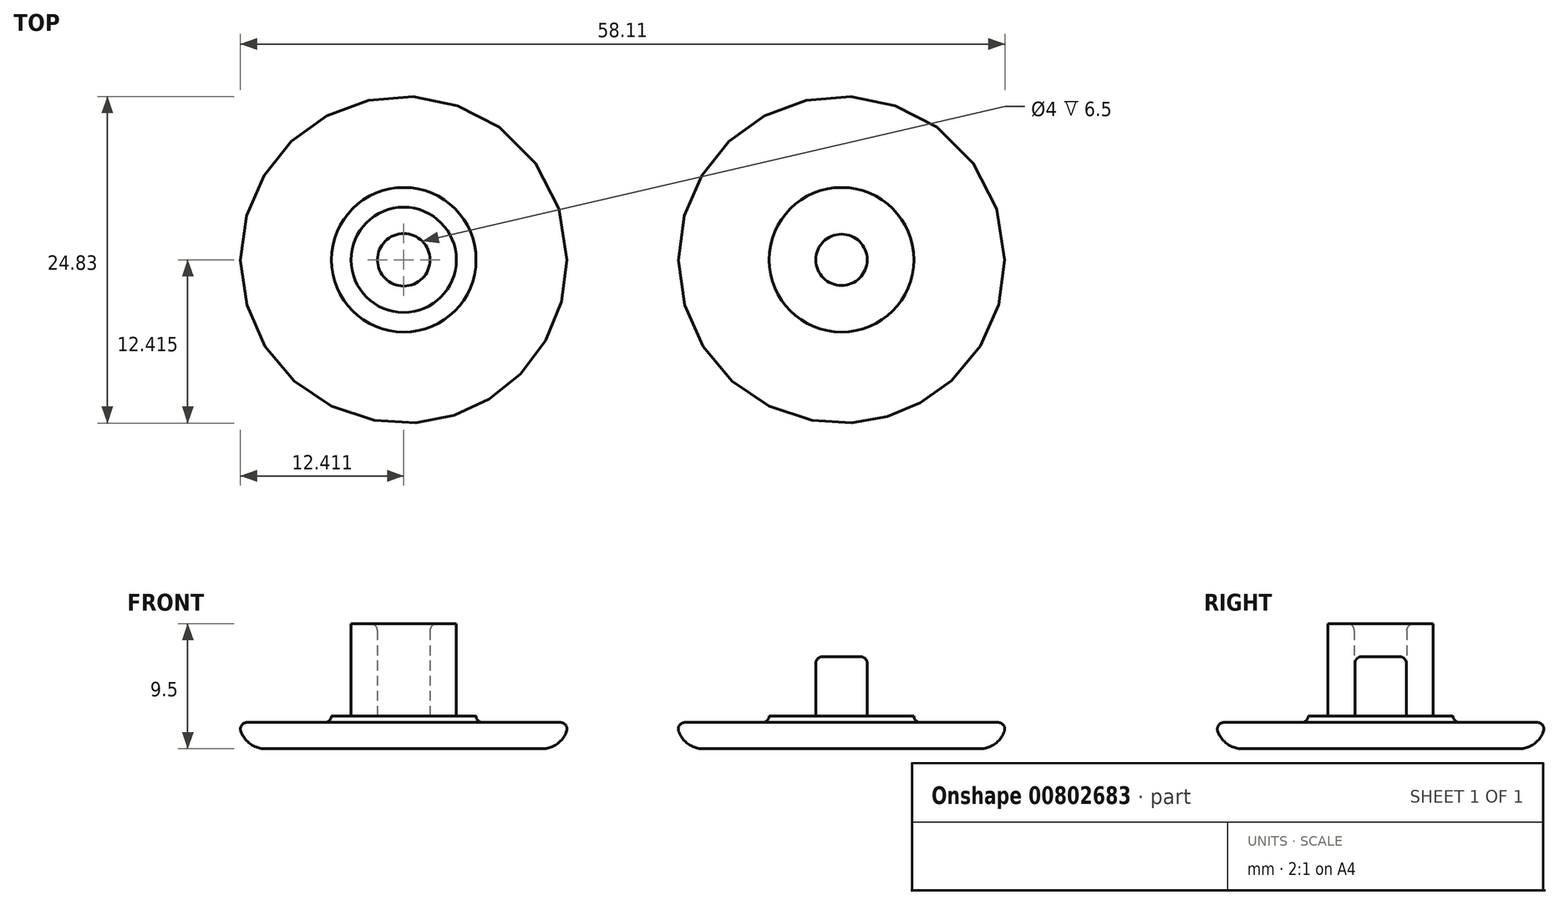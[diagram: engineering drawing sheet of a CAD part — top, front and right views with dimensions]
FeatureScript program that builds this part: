
annotation { "Feature Type Name" : "Feature", "Feature Type Description" : "" }
export const myFeature = defineFeature(function(context is Context, id is Id, definition is map)
    precondition{}
    {
        {
            var Q0;
            Q0=qCreatedBy(makeId("Top.planeOp"),FACE);
            var sketch = newSketch(context, id + "F0", { "sketchPlane" : qUnion([Q0])});
            skCircle(sketch, "E0", {"center": v(-165.76, 137.5) * mm, "radius": 12.5 * mm});
            skCircle(sketch, "E1", {"center": v(-132.48, 137.5) * mm, "radius": 12.5 * mm});
            skCircle(sketch, "E2", {"center": v(-165.76, 137.5) * mm, "radius": 5.5 * mm});
            skCircle(sketch, "E3", {"center": v(-165.76, 137.5) * mm, "radius": 4 * mm});
            skCircle(sketch, "E4", {"center": v(-165.76, 137.5) * mm, "radius": 2 * mm});
            skCircle(sketch, "E5", {"center": v(-132.48, 137.5) * mm, "radius": 5.5 * mm});
            skCircle(sketch, "E6", {"center": v(-132.48, 137.5) * mm, "radius": 1.95 * mm});
            skSolve(sketch);
        }
        {
            var Q0;
            Q0=makeQuery(id+"F0.imprint","IMPRINT",FACE,{"disambiguationData":[TD([[makeQuery(id+"F0.imprint","IMPRINT",EDGE,{"derivedFrom":sQuery(id+"F0.wireOp",EDGE,"E0")}),1.0]])]});
            var Q1;
            Q1=makeQuery(id+"F0.imprint","IMPRINT",FACE,{"disambiguationData":[TD([[makeQuery(id+"F0.imprint","IMPRINT",EDGE,{"derivedFrom":sQuery(id+"F0.wireOp",EDGE,"E1")}),1.0]])]});
            extrude(context, id + "F1", {"entities" : qUnion([Q0, Q1]), "depth" : 2 * mm, "offsetDistance" : 25 * mm});
        }
        {
            var Q0;
            Q0=makeQuery(id+"F0.imprint","IMPRINT",FACE,{"disambiguationData":[TD([[makeQuery(id+"F0.imprint","IMPRINT",EDGE,{"derivedFrom":sQuery(id+"F0.wireOp",EDGE,"E2")}),1.0]])]});
            var Q1;
            Q1=makeQuery(id+"F0.imprint","IMPRINT",FACE,{"disambiguationData":[TD([[makeQuery(id+"F0.imprint","IMPRINT",EDGE,{"derivedFrom":sQuery(id+"F0.wireOp",EDGE,"E5")}),1.0]])]});
            var Q2;
            Q2=makeQuery(id+"F0.imprint","IMPRINT",FACE,{"disambiguationData":[TD([[makeQuery(id+"F0.imprint","IMPRINT",EDGE,{"derivedFrom":sQuery(id+"F0.wireOp",EDGE,"E4")}),1.0]])]});
            extrude(context, id + "F2", {"entities" : qUnion([Q0, Q1, Q2]), "depth" : 2.5 * mm, "offsetDistance" : 25 * mm});
        }
        {
            var Q0;
            Q0=makeQuery(id+"F0.imprint","IMPRINT",FACE,{"disambiguationData":[TD([[makeQuery(id+"F0.imprint","IMPRINT",EDGE,{"derivedFrom":sQuery(id+"F0.wireOp",EDGE,"E3")}),1.0]])]});
            extrude(context, id + "F3", {"entities" : qUnion([Q0]), "depth" : 9.5 * mm, "offsetDistance" : 25 * mm});
        }
        {
            var Q0;
            Q0=makeQuery(id+"F0.imprint","IMPRINT",FACE,{"disambiguationData":[TD([[makeQuery(id+"F0.imprint","IMPRINT",EDGE,{"derivedFrom":sQuery(id+"F0.wireOp",EDGE,"E6")}),1.0]])]});
            extrude(context, id + "F4", {"entities" : qUnion([Q0]), "operationType" : NewBodyOperationType.ADD, "depth" : 7 * mm, "offsetDistance" : 25 * mm});
        }
        {
            var Q0;
            Q0=makeQuery(id+"F3.opExtrude","SWEPT_BODY",BODY,{"disambiguationData":[OSD([sQuery(id+"F0.wireOp",EDGE,"E3"),sQuery(id+"F0.wireOp",EDGE,"E4")])]});
            var Q1;
            Q1=makeQuery(id+"F2.opExtrude","SWEPT_BODY",BODY,{"disambiguationData":[OSD([sQuery(id+"F0.wireOp",EDGE,"E4")])]});
            var Q2;
            Q2=makeQuery(id+"F1.opExtrude","SWEPT_BODY",BODY,{"disambiguationData":[OSD([sQuery(id+"F0.wireOp",EDGE,"E0"),sQuery(id+"F0.wireOp",EDGE,"E2")])]});
            var Q3;
            Q3=makeQuery(id+"F2.opExtrude","SWEPT_BODY",BODY,{"disambiguationData":[OSD([sQuery(id+"F0.wireOp",EDGE,"E2"),sQuery(id+"F0.wireOp",EDGE,"E3")])]});
            booleanBodies(context, id + "F5", {"operationType" : BooleanOperationType.UNION, "tools" : qUnion([Q0, Q1, Q2, Q3])});
        }
        {
            var Q0;
            Q0=makeQuery(id+"F3.opExtrude","SWEPT_BODY",BODY,{"disambiguationData":[OSD([sQuery(id+"F0.wireOp",EDGE,"E6")])]});
            var Q1;
            Q1=makeQuery(id+"F2.opExtrude","SWEPT_BODY",BODY,{"disambiguationData":[OSD([sQuery(id+"F0.wireOp",EDGE,"E5"),sQuery(id+"F0.wireOp",EDGE,"E6")])]});
            var Q2;
            Q2=makeQuery(id+"F1.opExtrude","SWEPT_BODY",BODY,{"disambiguationData":[OSD([sQuery(id+"F0.wireOp",EDGE,"E1"),sQuery(id+"F0.wireOp",EDGE,"E5")])]});
            booleanBodies(context, id + "F6", {"operationType" : BooleanOperationType.UNION, "tools" : qUnion([Q0, Q1, Q2])});
        }
        {
            var Q0;
            {var subQ0=sQuery(id+"F0.wireOp",EDGE,"E6");var subQ1=sQuery(id+"F0.wireOp",EDGE,"E5");Q0=makeQuery(id+"F6.opBoolean","MERGE",FACE,{"derivedFrom":[makeQuery(id+"F1.opExtrude","CAP_FACE",FACE,{"disambiguationData":[OSD([sQuery(id+"F0.wireOp",EDGE,"E1"),subQ1])],"isStart":true}),makeQuery(id+"F2.opExtrude","CAP_FACE",FACE,{"disambiguationData":[OSD([subQ1,subQ0])],"isStart":true}),makeQuery(id+"F3.opExtrude","CAP_FACE",FACE,{"disambiguationData":[OSD([subQ0])],"isStart":true})]});}
            var Q1;
            {var subQ0=sQuery(id+"F0.wireOp",EDGE,"E4");var subQ1=sQuery(id+"F0.wireOp",EDGE,"E3");var subQ2=sQuery(id+"F0.wireOp",EDGE,"E2");Q1=makeQuery(id+"F5.opBoolean","MERGE",FACE,{"derivedFrom":[makeQuery(id+"F1.opExtrude","CAP_FACE",FACE,{"disambiguationData":[OSD([sQuery(id+"F0.wireOp",EDGE,"E0"),subQ2])],"isStart":true}),makeQuery(id+"F2.opExtrude","CAP_FACE",FACE,{"disambiguationData":[OSD([subQ2,subQ1])],"isStart":true}),makeQuery(id+"F2.opExtrude","CAP_FACE",FACE,{"disambiguationData":[OSD([subQ0])],"isStart":true}),makeQuery(id+"F3.opExtrude","CAP_FACE",FACE,{"disambiguationData":[OSD([subQ1,subQ0])],"isStart":true})]});}
            fillet(context, id + "F7", {"entities" : qUnion([Q0, Q1]), "radius" : 2 * mm, "tangentPropagation" : true, "allowEdgeOverflow" : false});
        }
        {
            var Q0;
            Q0=makeQuery(id+"F1.opExtrude","CAP_FACE",FACE,{"disambiguationData":[OSD([sQuery(id+"F0.wireOp",EDGE,"E0"),sQuery(id+"F0.wireOp",EDGE,"E2")])],"isStart":false});
            var Q1;
            Q1=makeQuery(id+"F1.opExtrude","CAP_FACE",FACE,{"disambiguationData":[OSD([sQuery(id+"F0.wireOp",EDGE,"E1"),sQuery(id+"F0.wireOp",EDGE,"E5")])],"isStart":false});
            var Q2;
            Q2=makeQuery(id+"F4.opExtrude","CAP_EDGE",EDGE,{"disambiguationData":[OSD([sQuery(id+"F0.wireOp",EDGE,"E6")])],"isStart":false});
            var Q3;
            Q3=makeQuery(id+"F3.opExtrude","CAP_EDGE",EDGE,{"disambiguationData":[OSD([sQuery(id+"F0.wireOp",EDGE,"E4")])],"isStart":false});
            fillet(context, id + "F8", {"entities" : qUnion([Q0, Q1, Q2, Q3]), "radius" : .5 * mm, "tangentPropagation" : true, "allowEdgeOverflow" : false});
        }
    });
